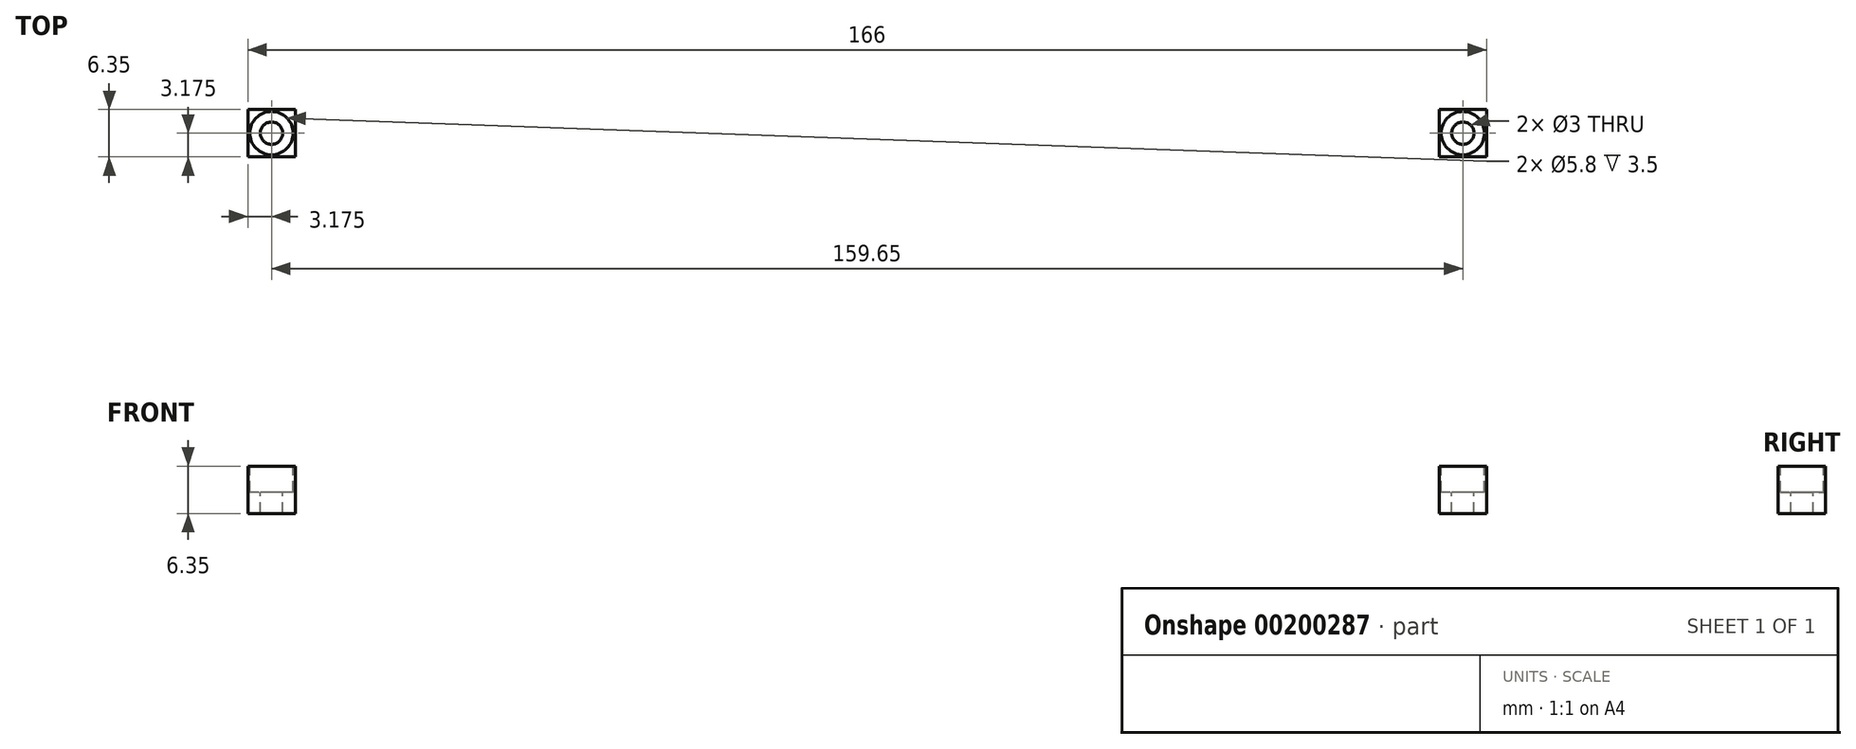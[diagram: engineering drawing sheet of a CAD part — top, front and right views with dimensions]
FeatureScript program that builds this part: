
annotation { "Feature Type Name" : "Feature", "Feature Type Description" : "" }
export const myFeature = defineFeature(function(context is Context, id is Id, definition is map)
    precondition{}
    {
        {
            var Q0;
            Q0=qCreatedBy(makeId("Top.planeOp"),FACE);
            var sketch = newSketch(context, id + "F0", { "sketchPlane" : qUnion([Q0])});
            skLineSegment(sketch, "E0.bottom", {"start": v(83, -21.5) * mm, "end": v(-83, -21.5) * mm});
            skPoint(sketch, "E0.middle", {"position": v(0, 0) * mm});
            skLineSegment(sketch, "E1.top", {"start": v(72.5, 14.5) * mm, "end": v(71.5, 14.5) * mm});
            skLineSegment(sketch, "E2", {"start": v(66.5, 14.5) * mm, "end": v(66.5, 12.75) * mm});
            skLineSegment(sketch, "E3", {"start": v(-72.5, 14.5) * mm, "end": v(-72.5, 12.75) * mm});
            skLineSegment(sketch, "E4", {"start": v(-71.5, 14.5) * mm, "end": v(-71.5, 12.75) * mm});
            skLineSegment(sketch, "E5", {"start": v(-66.5, 14.5) * mm, "end": v(-66.5, 12.75) * mm});
            skLineSegment(sketch, "E6", {"start": v(-65.5, 14.5) * mm, "end": v(-65.5, 12.75) * mm});
            skLineSegment(sketch, "E7", {"start": v(-60.5, 14.5) * mm, "end": v(-60.5, 12.75) * mm});
            skLineSegment(sketch, "E8", {"start": v(-59.5, 14.5) * mm, "end": v(-59.5, 12.75) * mm});
            skLineSegment(sketch, "E9", {"start": v(-54.5, 14.5) * mm, "end": v(-54.5, 12.75) * mm});
            skLineSegment(sketch, "E10", {"start": v(-53.5, 14.5) * mm, "end": v(-53.5, 12.75) * mm});
            skLineSegment(sketch, "E11", {"start": v(-48.5, 14.5) * mm, "end": v(-48.5, 12.75) * mm});
            skLineSegment(sketch, "E12", {"start": v(-47.5, 14.5) * mm, "end": v(-47.5, 12.75) * mm});
            skLineSegment(sketch, "E13", {"start": v(-42.5, 14.5) * mm, "end": v(-42.5, 12.75) * mm});
            skLineSegment(sketch, "E14", {"start": v(-41.5, 14.5) * mm, "end": v(-41.5, 12.75) * mm});
            skLineSegment(sketch, "E15", {"start": v(-36.5, 14.5) * mm, "end": v(-36.5, 12.75) * mm});
            skLineSegment(sketch, "E16", {"start": v(-35.5, 14.5) * mm, "end": v(-35.5, 12.75) * mm});
            skLineSegment(sketch, "E17", {"start": v(-30.5, 14.5) * mm, "end": v(-30.5, 12.75) * mm});
            skLineSegment(sketch, "E18", {"start": v(-29.5, 14.5) * mm, "end": v(-29.5, 12.75) * mm});
            skLineSegment(sketch, "E19", {"start": v(-24.5, 14.5) * mm, "end": v(-24.5, 12.75) * mm});
            skLineSegment(sketch, "E20", {"start": v(-23.5, 14.5) * mm, "end": v(-23.5, 12.75) * mm});
            skLineSegment(sketch, "E21", {"start": v(-18.5, 14.5) * mm, "end": v(-18.5, 12.75) * mm});
            skLineSegment(sketch, "E22", {"start": v(-17.5, 14.5) * mm, "end": v(-17.5, 12.75) * mm});
            skLineSegment(sketch, "E23", {"start": v(-12.5, 14.5) * mm, "end": v(-12.5, 12.75) * mm});
            skLineSegment(sketch, "E24", {"start": v(-11.5, 14.5) * mm, "end": v(-11.5, 12.75) * mm});
            skLineSegment(sketch, "E25", {"start": v(-6.5, 14.5) * mm, "end": v(-6.5, 12.75) * mm});
            skLineSegment(sketch, "E26", {"start": v(-5.5, 14.5) * mm, "end": v(-5.5, 12.75) * mm});
            skLineSegment(sketch, "E27", {"start": v(-0.5, 14.5) * mm, "end": v(-0.5, 12.75) * mm});
            skLineSegment(sketch, "E28", {"start": v(0.5, 14.5) * mm, "end": v(0.5, 12.75) * mm});
            skLineSegment(sketch, "E29", {"start": v(5.5, 14.5) * mm, "end": v(5.5, 12.75) * mm});
            skLineSegment(sketch, "E30", {"start": v(6.5, 14.5) * mm, "end": v(6.5, 12.75) * mm});
            skLineSegment(sketch, "E31", {"start": v(11.5, 14.5) * mm, "end": v(11.5, 12.75) * mm});
            skLineSegment(sketch, "E32", {"start": v(12.5, 14.5) * mm, "end": v(12.5, 12.75) * mm});
            skLineSegment(sketch, "E33", {"start": v(17.5, 14.5) * mm, "end": v(17.5, 12.75) * mm});
            skLineSegment(sketch, "E34", {"start": v(18.5, 14.5) * mm, "end": v(18.5, 12.75) * mm});
            skLineSegment(sketch, "E35", {"start": v(23.5, 14.5) * mm, "end": v(23.5, 12.75) * mm});
            skLineSegment(sketch, "E36", {"start": v(24.5, 14.5) * mm, "end": v(24.5, 12.75) * mm});
            skLineSegment(sketch, "E37", {"start": v(29.5, 14.5) * mm, "end": v(29.5, 12.75) * mm});
            skLineSegment(sketch, "E38", {"start": v(30.5, 14.5) * mm, "end": v(30.5, 12.75) * mm});
            skLineSegment(sketch, "E39", {"start": v(35.5, 14.5) * mm, "end": v(35.5, 12.75) * mm});
            skLineSegment(sketch, "E40", {"start": v(36.5, 14.5) * mm, "end": v(36.5, 12.75) * mm});
            skLineSegment(sketch, "E41", {"start": v(42.5, 14.5) * mm, "end": v(42.5, 12.75) * mm});
            skLineSegment(sketch, "E42", {"start": v(47.5, 14.5) * mm, "end": v(47.5, 12.75) * mm});
            skLineSegment(sketch, "E43", {"start": v(53.5, 14.5) * mm, "end": v(53.5, 12.75) * mm});
            skLineSegment(sketch, "E44", {"start": v(54.5, 14.5) * mm, "end": v(54.5, 12.75) * mm});
            skLineSegment(sketch, "E45", {"start": v(60.5, 14.5) * mm, "end": v(60.5, 12.75) * mm});
            skLineSegment(sketch, "E46", {"start": v(65.5, 14.5) * mm, "end": v(65.5, 12.75) * mm});
            skLineSegment(sketch, "E47", {"start": v(41.5, 14.5) * mm, "end": v(41.5, 12.75) * mm});
            skLineSegment(sketch, "E48", {"start": v(48.5, 14.5) * mm, "end": v(48.5, 12.75) * mm});
            skLineSegment(sketch, "E49", {"start": v(59.5, 14.5) * mm, "end": v(59.5, 12.75) * mm});
            skLineSegment(sketch, "E50", {"start": v(71.5, 14.5) * mm, "end": v(71.5, 12.75) * mm});
            skLineSegment(sketch, "E51", {"start": v(72.5, 14.5) * mm, "end": v(72.5, 12.75) * mm});
            skLineSegment(sketch, "E52.trimOffspring", {"start": v(-72.5, -12.75) * mm, "end": v(-72.5, -14.5) * mm});
            skLineSegment(sketch, "E53.trimOffspring", {"start": v(-71.5, -12.75) * mm, "end": v(-71.5, -14.5) * mm});
            skLineSegment(sketch, "E54.trimOffspring", {"start": v(-66.5, -12.75) * mm, "end": v(-66.5, -14.5) * mm});
            skLineSegment(sketch, "E55.trimOffspring", {"start": v(-65.5, -12.75) * mm, "end": v(-65.5, -14.5) * mm});
            skLineSegment(sketch, "E56.trimOffspring", {"start": v(-60.5, -12.75) * mm, "end": v(-60.5, -14.5) * mm});
            skLineSegment(sketch, "E57.trimOffspring", {"start": v(-59.5, -12.75) * mm, "end": v(-59.5, -14.5) * mm});
            skLineSegment(sketch, "E58.trimOffspring", {"start": v(-54.5, -12.75) * mm, "end": v(-54.5, -14.5) * mm});
            skLineSegment(sketch, "E59.trimOffspring", {"start": v(-53.5, -12.75) * mm, "end": v(-53.5, -14.5) * mm});
            skLineSegment(sketch, "E60.trimOffspring", {"start": v(-48.5, -12.75) * mm, "end": v(-48.5, -14.5) * mm});
            skLineSegment(sketch, "E61.trimOffspring", {"start": v(-47.5, -12.75) * mm, "end": v(-47.5, -14.5) * mm});
            skLineSegment(sketch, "E62.trimOffspring", {"start": v(-42.5, -12.75) * mm, "end": v(-42.5, -14.5) * mm});
            skLineSegment(sketch, "E63.trimOffspring", {"start": v(-41.5, -12.75) * mm, "end": v(-41.5, -14.5) * mm});
            skLineSegment(sketch, "E64.trimOffspring", {"start": v(-36.5, -12.75) * mm, "end": v(-36.5, -14.5) * mm});
            skLineSegment(sketch, "E65.trimOffspring", {"start": v(-35.5, -12.75) * mm, "end": v(-35.5, -14.5) * mm});
            skLineSegment(sketch, "E66.trimOffspring", {"start": v(-30.5, -12.75) * mm, "end": v(-30.5, -14.5) * mm});
            skLineSegment(sketch, "E67.trimOffspring", {"start": v(-29.5, -12.75) * mm, "end": v(-29.5, -14.5) * mm});
            skLineSegment(sketch, "E68.trimOffspring", {"start": v(-24.5, -12.75) * mm, "end": v(-24.5, -14.5) * mm});
            skLineSegment(sketch, "E69.trimOffspring", {"start": v(-23.5, -12.75) * mm, "end": v(-23.5, -14.5) * mm});
            skLineSegment(sketch, "E70.trimOffspring", {"start": v(-18.5, -12.75) * mm, "end": v(-18.5, -14.5) * mm});
            skLineSegment(sketch, "E71.trimOffspring", {"start": v(-17.5, -12.75) * mm, "end": v(-17.5, -14.5) * mm});
            skLineSegment(sketch, "E72.trimOffspring", {"start": v(-12.5, -12.75) * mm, "end": v(-12.5, -14.5) * mm});
            skLineSegment(sketch, "E73.trimOffspring", {"start": v(-11.5, -12.75) * mm, "end": v(-11.5, -14.5) * mm});
            skLineSegment(sketch, "E74.trimOffspring", {"start": v(-6.5, -12.75) * mm, "end": v(-6.5, -14.5) * mm});
            skLineSegment(sketch, "E75.trimOffspring", {"start": v(-5.5, -12.75) * mm, "end": v(-5.5, -14.5) * mm});
            skLineSegment(sketch, "E76.trimOffspring", {"start": v(-0.5, -12.75) * mm, "end": v(-0.5, -14.5) * mm});
            skLineSegment(sketch, "E77.trimOffspring", {"start": v(0.5, -12.75) * mm, "end": v(0.5, -14.5) * mm});
            skLineSegment(sketch, "E78.trimOffspring", {"start": v(5.5, -12.75) * mm, "end": v(5.5, -14.5) * mm});
            skLineSegment(sketch, "E79.trimOffspring", {"start": v(6.5, -12.75) * mm, "end": v(6.5, -14.5) * mm});
            skLineSegment(sketch, "E80.trimOffspring", {"start": v(11.5, -12.75) * mm, "end": v(11.5, -14.5) * mm});
            skLineSegment(sketch, "E81.trimOffspring", {"start": v(12.5, -12.75) * mm, "end": v(12.5, -14.5) * mm});
            skLineSegment(sketch, "E82.trimOffspring", {"start": v(17.5, -12.75) * mm, "end": v(17.5, -14.5) * mm});
            skLineSegment(sketch, "E83.trimOffspring", {"start": v(18.5, -12.75) * mm, "end": v(18.5, -14.5) * mm});
            skLineSegment(sketch, "E84.trimOffspring", {"start": v(23.5, -12.75) * mm, "end": v(23.5, -14.5) * mm});
            skLineSegment(sketch, "E85.trimOffspring", {"start": v(24.5, -12.75) * mm, "end": v(24.5, -14.5) * mm});
            skLineSegment(sketch, "E86.trimOffspring", {"start": v(29.5, -12.75) * mm, "end": v(29.5, -14.5) * mm});
            skLineSegment(sketch, "E87.trimOffspring", {"start": v(30.5, -12.75) * mm, "end": v(30.5, -14.5) * mm});
            skLineSegment(sketch, "E88.trimOffspring", {"start": v(35.5, -12.75) * mm, "end": v(35.5, -14.5) * mm});
            skLineSegment(sketch, "E89.trimOffspring", {"start": v(36.5, -12.75) * mm, "end": v(36.5, -14.5) * mm});
            skLineSegment(sketch, "E90.trimOffspring", {"start": v(41.5, -12.75) * mm, "end": v(41.5, -14.5) * mm});
            skLineSegment(sketch, "E91.trimOffspring", {"start": v(42.5, -12.75) * mm, "end": v(42.5, -14.5) * mm});
            skLineSegment(sketch, "E92.trimOffspring", {"start": v(47.5, -12.75) * mm, "end": v(47.5, -14.5) * mm});
            skLineSegment(sketch, "E93.trimOffspring", {"start": v(48.5, -12.75) * mm, "end": v(48.5, -14.5) * mm});
            skLineSegment(sketch, "E94.trimOffspring", {"start": v(53.5, -12.75) * mm, "end": v(53.5, -14.5) * mm});
            skLineSegment(sketch, "E95.trimOffspring", {"start": v(54.5, -12.75) * mm, "end": v(54.5, -14.5) * mm});
            skLineSegment(sketch, "E96.trimOffspring", {"start": v(59.5, -12.75) * mm, "end": v(59.5, -14.5) * mm});
            skLineSegment(sketch, "E97.trimOffspring", {"start": v(60.5, -12.75) * mm, "end": v(60.5, -14.5) * mm});
            skLineSegment(sketch, "E98.trimOffspring", {"start": v(65.5, -12.75) * mm, "end": v(65.5, -14.5) * mm});
            skLineSegment(sketch, "E99.trimOffspring", {"start": v(66.5, -12.75) * mm, "end": v(66.5, -14.5) * mm});
            skLineSegment(sketch, "E100.trimOffspring", {"start": v(71.5, -12.75) * mm, "end": v(71.5, -14.5) * mm});
            skLineSegment(sketch, "E101.trimOffspring", {"start": v(72.5, -12.75) * mm, "end": v(72.5, -14.5) * mm});
            skLineSegment(sketch, "E102.trimOffspring", {"start": v(66.5, 12.75) * mm, "end": v(71.5, 12.75) * mm});
            skLineSegment(sketch, "E103.trimOffspring", {"start": v(60.5, 12.75) * mm, "end": v(65.5, 12.75) * mm});
            skLineSegment(sketch, "E104.trimOffspring", {"start": v(54.5, 12.75) * mm, "end": v(59.5, 12.75) * mm});
            skLineSegment(sketch, "E105.trimOffspring", {"start": v(48.5, 12.75) * mm, "end": v(53.5, 12.75) * mm});
            skLineSegment(sketch, "E106.trimOffspring", {"start": v(42.5, 12.75) * mm, "end": v(47.5, 12.75) * mm});
            skLineSegment(sketch, "E107.trimOffspring", {"start": v(36.5, 12.75) * mm, "end": v(41.5, 12.75) * mm});
            skLineSegment(sketch, "E108.trimOffspring", {"start": v(30.5, 12.75) * mm, "end": v(35.5, 12.75) * mm});
            skLineSegment(sketch, "E109.trimOffspring", {"start": v(24.5, 12.75) * mm, "end": v(29.5, 12.75) * mm});
            skLineSegment(sketch, "E110.trimOffspring", {"start": v(18.5, 12.75) * mm, "end": v(23.5, 12.75) * mm});
            skLineSegment(sketch, "E111.trimOffspring", {"start": v(12.5, 12.75) * mm, "end": v(17.5, 12.75) * mm});
            skLineSegment(sketch, "E112.trimOffspring", {"start": v(6.5, 12.75) * mm, "end": v(11.5, 12.75) * mm});
            skLineSegment(sketch, "E113.trimOffspring", {"start": v(0.5, 12.75) * mm, "end": v(5.5, 12.75) * mm});
            skLineSegment(sketch, "E114.trimOffspring", {"start": v(-5.5, 12.75) * mm, "end": v(-0.5, 12.75) * mm});
            skLineSegment(sketch, "E115.trimOffspring", {"start": v(-11.5, 12.75) * mm, "end": v(-6.5, 12.75) * mm});
            skLineSegment(sketch, "E116.trimOffspring", {"start": v(-17.5, 12.75) * mm, "end": v(-12.5, 12.75) * mm});
            skLineSegment(sketch, "E117.trimOffspring", {"start": v(-23.5, 12.75) * mm, "end": v(-18.5, 12.75) * mm});
            skLineSegment(sketch, "E118.trimOffspring", {"start": v(-29.5, 12.75) * mm, "end": v(-24.5, 12.75) * mm});
            skLineSegment(sketch, "E119.trimOffspring", {"start": v(-35.5, 12.75) * mm, "end": v(-30.5, 12.75) * mm});
            skLineSegment(sketch, "E120.trimOffspring", {"start": v(-41.5, 12.75) * mm, "end": v(-36.5, 12.75) * mm});
            skLineSegment(sketch, "E121.trimOffspring", {"start": v(-47.5, 12.75) * mm, "end": v(-42.5, 12.75) * mm});
            skLineSegment(sketch, "E122.trimOffspring", {"start": v(-53.5, 12.75) * mm, "end": v(-48.5, 12.75) * mm});
            skLineSegment(sketch, "E123.trimOffspring", {"start": v(-59.5, 12.75) * mm, "end": v(-54.5, 12.75) * mm});
            skLineSegment(sketch, "E124.trimOffspring", {"start": v(-65.5, 12.75) * mm, "end": v(-60.5, 12.75) * mm});
            skLineSegment(sketch, "E125.trimOffspring", {"start": v(-71.5, 12.75) * mm, "end": v(-66.5, 12.75) * mm});
            skLineSegment(sketch, "E126.trimOffspring", {"start": v(-71.5, -12.75) * mm, "end": v(-66.5, -12.75) * mm});
            skLineSegment(sketch, "E127.trimOffspring", {"start": v(-71.5, -14.5) * mm, "end": v(-72.5, -14.5) * mm});
            skLineSegment(sketch, "E128.trimOffspring", {"start": v(-65.5, -12.75) * mm, "end": v(-60.5, -12.75) * mm});
            skLineSegment(sketch, "E129.trimOffspring", {"start": v(-65.5, -14.5) * mm, "end": v(-66.5, -14.5) * mm});
            skLineSegment(sketch, "E130.trimOffspring", {"start": v(-59.5, -12.75) * mm, "end": v(-54.5, -12.75) * mm});
            skLineSegment(sketch, "E131.trimOffspring", {"start": v(-59.5, -14.5) * mm, "end": v(-60.5, -14.5) * mm});
            skLineSegment(sketch, "E132.trimOffspring", {"start": v(-53.5, -12.75) * mm, "end": v(-48.5, -12.75) * mm});
            skLineSegment(sketch, "E133.trimOffspring", {"start": v(-53.5, -14.5) * mm, "end": v(-54.5, -14.5) * mm});
            skLineSegment(sketch, "E134.trimOffspring", {"start": v(-47.5, -12.75) * mm, "end": v(-42.5, -12.75) * mm});
            skLineSegment(sketch, "E135.trimOffspring", {"start": v(-47.5, -14.5) * mm, "end": v(-48.5, -14.5) * mm});
            skLineSegment(sketch, "E136.trimOffspring", {"start": v(-41.5, -12.75) * mm, "end": v(-36.5, -12.75) * mm});
            skLineSegment(sketch, "E137.trimOffspring", {"start": v(-41.5, -14.5) * mm, "end": v(-42.5, -14.5) * mm});
            skLineSegment(sketch, "E138.trimOffspring", {"start": v(-35.5, -12.75) * mm, "end": v(-30.5, -12.75) * mm});
            skLineSegment(sketch, "E139.trimOffspring", {"start": v(-35.5, -14.5) * mm, "end": v(-36.5, -14.5) * mm});
            skLineSegment(sketch, "E140.trimOffspring", {"start": v(-29.5, -12.75) * mm, "end": v(-24.5, -12.75) * mm});
            skLineSegment(sketch, "E141.trimOffspring", {"start": v(-29.5, -14.5) * mm, "end": v(-30.5, -14.5) * mm});
            skLineSegment(sketch, "E142.trimOffspring", {"start": v(-23.5, -12.75) * mm, "end": v(-18.5, -12.75) * mm});
            skLineSegment(sketch, "E143.trimOffspring", {"start": v(-23.5, -14.5) * mm, "end": v(-24.5, -14.5) * mm});
            skLineSegment(sketch, "E144.trimOffspring", {"start": v(-17.5, -12.75) * mm, "end": v(-12.5, -12.75) * mm});
            skLineSegment(sketch, "E145.trimOffspring", {"start": v(-17.5, -14.5) * mm, "end": v(-18.5, -14.5) * mm});
            skLineSegment(sketch, "E146.trimOffspring", {"start": v(-11.5, -12.75) * mm, "end": v(-6.5, -12.75) * mm});
            skLineSegment(sketch, "E147.trimOffspring", {"start": v(-11.5, -14.5) * mm, "end": v(-12.5, -14.5) * mm});
            skLineSegment(sketch, "E148.trimOffspring", {"start": v(-5.5, -12.75) * mm, "end": v(-0.5, -12.75) * mm});
            skLineSegment(sketch, "E149.trimOffspring", {"start": v(-5.5, -14.5) * mm, "end": v(-6.5, -14.5) * mm});
            skLineSegment(sketch, "E150.trimOffspring", {"start": v(0.5, -12.75) * mm, "end": v(5.5, -12.75) * mm});
            skLineSegment(sketch, "E151.trimOffspring", {"start": v(0.5, -14.5) * mm, "end": v(-0.5, -14.5) * mm});
            skLineSegment(sketch, "E152.trimOffspring", {"start": v(6.5, -12.75) * mm, "end": v(11.5, -12.75) * mm});
            skLineSegment(sketch, "E153.trimOffspring", {"start": v(6.5, -14.5) * mm, "end": v(5.5, -14.5) * mm});
            skLineSegment(sketch, "E154.trimOffspring", {"start": v(12.5, -12.75) * mm, "end": v(17.5, -12.75) * mm});
            skLineSegment(sketch, "E155.trimOffspring", {"start": v(12.5, -14.5) * mm, "end": v(11.5, -14.5) * mm});
            skLineSegment(sketch, "E156.trimOffspring", {"start": v(18.5, -12.75) * mm, "end": v(23.5, -12.75) * mm});
            skLineSegment(sketch, "E157.trimOffspring", {"start": v(24.5, -12.75) * mm, "end": v(29.5, -12.75) * mm});
            skLineSegment(sketch, "E158.trimOffspring", {"start": v(30.5, -12.75) * mm, "end": v(35.5, -12.75) * mm});
            skLineSegment(sketch, "E159.trimOffspring", {"start": v(36.5, -12.75) * mm, "end": v(41.5, -12.75) * mm});
            skLineSegment(sketch, "E160.trimOffspring", {"start": v(42.5, -12.75) * mm, "end": v(47.5, -12.75) * mm});
            skLineSegment(sketch, "E161.trimOffspring", {"start": v(48.5, -12.75) * mm, "end": v(53.5, -12.75) * mm});
            skLineSegment(sketch, "E162.trimOffspring", {"start": v(54.5, -12.75) * mm, "end": v(59.5, -12.75) * mm});
            skLineSegment(sketch, "E163.trimOffspring", {"start": v(60.5, -12.75) * mm, "end": v(65.5, -12.75) * mm});
            skLineSegment(sketch, "E164.trimOffspring", {"start": v(66.5, -12.75) * mm, "end": v(71.5, -12.75) * mm});
            skLineSegment(sketch, "E165.trimOffspring", {"start": v(66.5, -14.5) * mm, "end": v(65.5, -14.5) * mm});
            skLineSegment(sketch, "E166.trimOffspring", {"start": v(60.5, -14.5) * mm, "end": v(59.5, -14.5) * mm});
            skLineSegment(sketch, "E167", {"start": v(71.5, -14.5) * mm, "end": v(72.5, -14.5) * mm});
            skLineSegment(sketch, "E168.trimOffspring", {"start": v(54.5, -14.5) * mm, "end": v(53.5, -14.5) * mm});
            skLineSegment(sketch, "E169.trimOffspring", {"start": v(48.5, -14.5) * mm, "end": v(47.5, -14.5) * mm});
            skLineSegment(sketch, "E170.trimOffspring", {"start": v(42.5, -14.5) * mm, "end": v(41.5, -14.5) * mm});
            skLineSegment(sketch, "E171.trimOffspring", {"start": v(36.5, -14.5) * mm, "end": v(35.5, -14.5) * mm});
            skLineSegment(sketch, "E172.trimOffspring", {"start": v(30.5, -14.5) * mm, "end": v(29.5, -14.5) * mm});
            skLineSegment(sketch, "E173.trimOffspring", {"start": v(24.5, -14.5) * mm, "end": v(23.5, -14.5) * mm});
            skLineSegment(sketch, "E174.trimOffspring", {"start": v(18.5, -14.5) * mm, "end": v(17.5, -14.5) * mm});
            skLineSegment(sketch, "E175.trimOffspring", {"start": v(-71.5, 14.5) * mm, "end": v(-72.5, 14.5) * mm});
            skLineSegment(sketch, "E176.trimOffspring", {"start": v(-65.5, 14.5) * mm, "end": v(-66.5, 14.5) * mm});
            skLineSegment(sketch, "E177.trimOffspring", {"start": v(-59.5, 14.5) * mm, "end": v(-60.5, 14.5) * mm});
            skLineSegment(sketch, "E178.trimOffspring", {"start": v(-53.5, 14.5) * mm, "end": v(-54.5, 14.5) * mm});
            skLineSegment(sketch, "E179.trimOffspring", {"start": v(-47.5, 14.5) * mm, "end": v(-48.5, 14.5) * mm});
            skLineSegment(sketch, "E180.trimOffspring", {"start": v(-41.5, 14.5) * mm, "end": v(-42.5, 14.5) * mm});
            skLineSegment(sketch, "E181.trimOffspring", {"start": v(-35.5, 14.5) * mm, "end": v(-36.5, 14.5) * mm});
            skLineSegment(sketch, "E182.trimOffspring", {"start": v(-29.5, 14.5) * mm, "end": v(-30.5, 14.5) * mm});
            skLineSegment(sketch, "E183.trimOffspring", {"start": v(-23.5, 14.5) * mm, "end": v(-24.5, 14.5) * mm});
            skLineSegment(sketch, "E184.trimOffspring", {"start": v(-17.5, 14.5) * mm, "end": v(-18.5, 14.5) * mm});
            skLineSegment(sketch, "E185.trimOffspring", {"start": v(-11.5, 14.5) * mm, "end": v(-12.5, 14.5) * mm});
            skLineSegment(sketch, "E186.trimOffspring", {"start": v(-5.5, 14.5) * mm, "end": v(-6.5, 14.5) * mm});
            skLineSegment(sketch, "E187.trimOffspring", {"start": v(0.5, 14.5) * mm, "end": v(-0.5, 14.5) * mm});
            skLineSegment(sketch, "E188.trimOffspring", {"start": v(12.5, 14.5) * mm, "end": v(11.5, 14.5) * mm});
            skLineSegment(sketch, "E189.trimOffspring", {"start": v(18.5, 14.5) * mm, "end": v(17.5, 14.5) * mm});
            skLineSegment(sketch, "E190.trimOffspring", {"start": v(24.5, 14.5) * mm, "end": v(23.5, 14.5) * mm});
            skLineSegment(sketch, "E191.trimOffspring", {"start": v(30.5, 14.5) * mm, "end": v(29.5, 14.5) * mm});
            skLineSegment(sketch, "E192.trimOffspring", {"start": v(66.5, 14.5) * mm, "end": v(65.5, 14.5) * mm});
            skLineSegment(sketch, "E193.trimOffspring", {"start": v(60.5, 14.5) * mm, "end": v(59.5, 14.5) * mm});
            skLineSegment(sketch, "E194.trimOffspring", {"start": v(54.5, 14.5) * mm, "end": v(53.5, 14.5) * mm});
            skLineSegment(sketch, "E195.trimOffspring", {"start": v(48.5, 14.5) * mm, "end": v(47.5, 14.5) * mm});
            skLineSegment(sketch, "E196.trimOffspring", {"start": v(42.5, 14.5) * mm, "end": v(41.5, 14.5) * mm});
            skLineSegment(sketch, "E197.trimOffspring", {"start": v(36.5, 14.5) * mm, "end": v(35.5, 14.5) * mm});
            skPoint(sketch, "E198", {"position": v(0, 4.75) * mm});
            skPoint(sketch, "E199", {"position": v(0, -4.75) * mm});
            skLineSegment(sketch, "E200", {"start": v(5.5, 14.5) * mm, "end": v(6.5, 14.5) * mm});
            skLineSegment(sketch, "E201", {"start": v(-83, 21.5) * mm, "end": v(-83, -21.5) * mm});
            skLineSegment(sketch, "E202", {"start": v(83, 21.5) * mm, "end": v(83, -21.5) * mm});
            skLineSegment(sketch, "E203", {"start": v(-83, 21.5) * mm, "end": v(83, 21.5) * mm});
            skLineSegment(sketch, "E204", {"start": v(-76.65, 12.75) * mm, "end": v(-76.65, -12.75) * mm});
            skLineSegment(sketch, "E205", {"start": v(76.65, 12.75) * mm, "end": v(76.65, -12.75) * mm});
            skLineSegment(sketch, "E206", {"start": v(-72.5, 12.75) * mm, "end": v(-76.65, 12.75) * mm});
            skLineSegment(sketch, "E207", {"start": v(-72.5, -12.75) * mm, "end": v(-76.65, -12.75) * mm});
            skLineSegment(sketch, "E208", {"start": v(72.5, 12.75) * mm, "end": v(76.65, 12.75) * mm});
            skLineSegment(sketch, "E209", {"start": v(72.5, -12.75) * mm, "end": v(76.65, -12.75) * mm});
            skPoint(sketch, "E210.orphan", {"position": v(-76.65, 21.5) * mm});
            skPoint(sketch, "E211.orphan", {"position": v(76.65, 21.5) * mm});
            skLineSegment(sketch, "E212.bottom", {"start": v(-83, 21.5) * mm, "end": v(-76.65, 21.5) * mm});
            skLineSegment(sketch, "E212.top", {"start": v(-83, 15.15) * mm, "end": v(-76.65, 15.15) * mm});
            skLineSegment(sketch, "E212.left", {"start": v(-83, 21.5) * mm, "end": v(-83, 15.15) * mm});
            skLineSegment(sketch, "E212.right", {"start": v(-76.65, 21.5) * mm, "end": v(-76.65, 15.15) * mm});
            skLineSegment(sketch, "E213.bottom", {"start": v(-83, -21.5) * mm, "end": v(-76.65, -21.5) * mm});
            skLineSegment(sketch, "E213.top", {"start": v(-83, -15.15) * mm, "end": v(-76.65, -15.15) * mm});
            skLineSegment(sketch, "E213.left", {"start": v(-83, -21.5) * mm, "end": v(-83, -15.15) * mm});
            skLineSegment(sketch, "E213.right", {"start": v(-76.65, -21.5) * mm, "end": v(-76.65, -15.15) * mm});
            skLineSegment(sketch, "E214.bottom", {"start": v(83, 21.5) * mm, "end": v(76.65, 21.5) * mm});
            skLineSegment(sketch, "E214.top", {"start": v(83, 15.15) * mm, "end": v(76.65, 15.15) * mm});
            skLineSegment(sketch, "E214.left", {"start": v(83, 21.5) * mm, "end": v(83, 15.15) * mm});
            skLineSegment(sketch, "E214.right", {"start": v(76.65, 21.5) * mm, "end": v(76.65, 15.15) * mm});
            skLineSegment(sketch, "E215.bottom", {"start": v(83, -21.5) * mm, "end": v(76.65, -21.5) * mm});
            skLineSegment(sketch, "E215.top", {"start": v(83, -15.15) * mm, "end": v(76.65, -15.15) * mm});
            skLineSegment(sketch, "E215.left", {"start": v(83, -21.5) * mm, "end": v(83, -15.15) * mm});
            skLineSegment(sketch, "E215.right", {"start": v(76.65, -21.5) * mm, "end": v(76.65, -15.15) * mm});
            skPoint(sketch, "E216", {"position": v(-79.83, 18.32) * mm});
            skPoint(sketch, "E216.positionSnap0", {"position": v(-83, 18.32) * mm});
            skPoint(sketch, "E216.positionSnap1", {"position": v(-79.83, 21.5) * mm});
            skPoint(sketch, "E217", {"position": v(-79.82, -18.33) * mm});
            skPoint(sketch, "E217.positionSnap0", {"position": v(-83, -18.33) * mm});
            skPoint(sketch, "E217.positionSnap1", {"position": v(-79.82, -21.5) * mm});
            skPoint(sketch, "E218", {"position": v(79.83, 18.33) * mm});
            skPoint(sketch, "E218.positionSnap0", {"position": v(79.83, 21.5) * mm});
            skPoint(sketch, "E218.positionSnap1", {"position": v(83, 18.33) * mm});
            skPoint(sketch, "E219", {"position": v(79.83, -18.32) * mm});
            skPoint(sketch, "E219.positionSnap0", {"position": v(79.83, -21.5) * mm});
            skPoint(sketch, "E219.positionSnap1", {"position": v(83, -18.32) * mm});
            skSolve(sketch);
        }
        {
            var Q0;
            Q0=makeQuery(id+"F0.imprint","IMPRINT",FACE,{"disambiguationData":[TD([[makeQuery(id+"F0.imprint","IMPRINT",EDGE,{"derivedFrom":sQuery(id+"F0.wireOp",EDGE,"E0.bottom")}),-1.0]])]});
            var Q1;
            Q1=makeQuery(id+"F0.imprint","IMPRINT",FACE,{"disambiguationData":[TD([[makeQuery(id+"F0.imprint","IMPRINT",EDGE,{"derivedFrom":sQuery(id+"F0.wireOp",EDGE,"K6HQALcg-SJ6E-UbpV-g3pM-SsoFJaYyiFHH.bottom")}),-1.0]])]});
            var Q2;
            Q2=makeQuery(id+"F0.imprint","IMPRINT",FACE,{"disambiguationData":[TD([[makeQuery(id+"F0.imprint","IMPRINT",EDGE,{"derivedFrom":sQuery(id+"F0.wireOp",EDGE,"uAhlTMjh-OfK6-l1ir-Uiju-3nNvoJU6ebrF.bottom")}),1.0]])]});
            var Q3;
            Q3=makeQuery(id+"F0.imprint","IMPRINT",FACE,{"disambiguationData":[TD([[makeQuery(id+"F0.imprint","IMPRINT",EDGE,{"derivedFrom":sQuery(id+"F0.wireOp",EDGE,"429Vr5qv-e7wW-sgXi-vds3-SuZLJVXfNGyf.bottom")}),1.0]])]});
            var Q4;
            Q4=makeQuery(id+"F0.imprint","IMPRINT",FACE,{"disambiguationData":[TD([[makeQuery(id+"F0.imprint","IMPRINT",EDGE,{"derivedFrom":sQuery(id+"F0.wireOp",EDGE,"gyryeJMz-dnlH-ok6h-gJO2-PR3vbfRycGDr.bottom")}),-1.0]])]});
            var Q5;
            Q5=makeQuery(id+"F0.imprint","IMPRINT",FACE,{"disambiguationData":[TD([[makeQuery(id+"F0.imprint","IMPRINT",EDGE,{"derivedFrom":sQuery(id+"F0.wireOp",EDGE,"Y8WRlr66-7ynR-SeF8-deyW-E6T64acYDO3Z")}),-1.0]])]});
            var Q6;
            Q6=makeQuery(id+"F0.imprint","IMPRINT",FACE,{"disambiguationData":[TD([[makeQuery(id+"F0.imprint","IMPRINT",EDGE,{"derivedFrom":sQuery(id+"F0.wireOp",EDGE,"CmYglgzX-7el8-TEhF-yuX0-v4MmdMN9OrBr")}),-1.0]])]});
            var Q7;
            Q7=makeQuery(id+"F0.imprint","IMPRINT",FACE,{"disambiguationData":[TD([[makeQuery(id+"F0.imprint","IMPRINT",EDGE,{"derivedFrom":sQuery(id+"F0.wireOp",EDGE,"HYskgT41-gjKB-VkVM-H0Av-PifG51DztXFj")}),1.0]])]});
            var Q8;
            Q8=makeQuery(id+"F0.imprint","IMPRINT",FACE,{"disambiguationData":[TD([[makeQuery(id+"F0.imprint","IMPRINT",EDGE,{"derivedFrom":sQuery(id+"F0.wireOp",EDGE,"VJJEuZ6N-K9C8-7fmf-kXEK-6F0NHCstAFbI")}),1.0]])]});
            var Q9;
            Q9=makeQuery(id+"F0.imprint","IMPRINT",FACE,{"disambiguationData":[TD([[makeQuery(id+"F0.imprint","IMPRINT",EDGE,{"derivedFrom":sQuery(id+"F0.wireOp",EDGE,"E212.bottom")}),-1.0]])]});
            var Q10;
            Q10=makeQuery(id+"F0.imprint","IMPRINT",FACE,{"disambiguationData":[TD([[makeQuery(id+"F0.imprint","IMPRINT",EDGE,{"derivedFrom":sQuery(id+"F0.wireOp",EDGE,"E213.bottom")}),1.0]])]});
            var Q11;
            Q11=makeQuery(id+"F0.imprint","IMPRINT",FACE,{"disambiguationData":[TD([[makeQuery(id+"F0.imprint","IMPRINT",EDGE,{"derivedFrom":sQuery(id+"F0.wireOp",EDGE,"E215.bottom")}),-1.0]])]});
            var Q12;
            Q12=makeQuery(id+"F0.imprint","IMPRINT",FACE,{"disambiguationData":[TD([[makeQuery(id+"F0.imprint","IMPRINT",EDGE,{"derivedFrom":sQuery(id+"F0.wireOp",EDGE,"E214.bottom")}),1.0]])]});
            extrude(context, id + "F1", {"entities" : qUnion([Q0, Q1, Q2, Q3, Q4, Q5, Q6, Q7, Q8, Q9, Q10, Q11, Q12]), "oppositeDirection" : true, "depth" : 6.35 * mm});
        }
        {
            var Q0;
            Q0=sQuery(id+"F0.wireOp",VERTEX,"E216");
            var Q1;
            Q1=sQuery(id+"F0.wireOp",VERTEX,"E217");
            var Q2;
            Q2=sQuery(id+"F0.wireOp",VERTEX,"E218");
            var Q3;
            Q3=sQuery(id+"F0.wireOp",VERTEX,"E219");
            var Q4;
            Q4=makeQuery(id+"F1.opExtrude","SWEPT_BODY",BODY,{"disambiguationData":[OSD([sQuery(id+"F0.wireOp",EDGE,"E0.bottom"),sQuery(id+"F0.wireOp",EDGE,"E1.top"),sQuery(id+"F0.wireOp",EDGE,"E2"),sQuery(id+"F0.wireOp",EDGE,"E3"),sQuery(id+"F0.wireOp",EDGE,"E4"),sQuery(id+"F0.wireOp",EDGE,"E5"),sQuery(id+"F0.wireOp",EDGE,"E6"),sQuery(id+"F0.wireOp",EDGE,"E7"),sQuery(id+"F0.wireOp",EDGE,"E8"),sQuery(id+"F0.wireOp",EDGE,"E9"),sQuery(id+"F0.wireOp",EDGE,"E10"),sQuery(id+"F0.wireOp",EDGE,"E11"),sQuery(id+"F0.wireOp",EDGE,"E12"),sQuery(id+"F0.wireOp",EDGE,"E13"),sQuery(id+"F0.wireOp",EDGE,"E14"),sQuery(id+"F0.wireOp",EDGE,"E15"),sQuery(id+"F0.wireOp",EDGE,"E16"),sQuery(id+"F0.wireOp",EDGE,"E17"),sQuery(id+"F0.wireOp",EDGE,"E18"),sQuery(id+"F0.wireOp",EDGE,"E19"),sQuery(id+"F0.wireOp",EDGE,"E20"),sQuery(id+"F0.wireOp",EDGE,"E21"),sQuery(id+"F0.wireOp",EDGE,"E22"),sQuery(id+"F0.wireOp",EDGE,"E23"),sQuery(id+"F0.wireOp",EDGE,"E24"),sQuery(id+"F0.wireOp",EDGE,"E25"),sQuery(id+"F0.wireOp",EDGE,"E26"),sQuery(id+"F0.wireOp",EDGE,"E27"),sQuery(id+"F0.wireOp",EDGE,"E28"),sQuery(id+"F0.wireOp",EDGE,"E29"),sQuery(id+"F0.wireOp",EDGE,"E30"),sQuery(id+"F0.wireOp",EDGE,"E31"),sQuery(id+"F0.wireOp",EDGE,"E32"),sQuery(id+"F0.wireOp",EDGE,"E33"),sQuery(id+"F0.wireOp",EDGE,"E34"),sQuery(id+"F0.wireOp",EDGE,"E35"),sQuery(id+"F0.wireOp",EDGE,"E36"),sQuery(id+"F0.wireOp",EDGE,"E37"),sQuery(id+"F0.wireOp",EDGE,"E38"),sQuery(id+"F0.wireOp",EDGE,"E39"),sQuery(id+"F0.wireOp",EDGE,"E40"),sQuery(id+"F0.wireOp",EDGE,"E41"),sQuery(id+"F0.wireOp",EDGE,"E42"),sQuery(id+"F0.wireOp",EDGE,"E43"),sQuery(id+"F0.wireOp",EDGE,"E44"),sQuery(id+"F0.wireOp",EDGE,"E45"),sQuery(id+"F0.wireOp",EDGE,"E46"),sQuery(id+"F0.wireOp",EDGE,"E47"),sQuery(id+"F0.wireOp",EDGE,"E48"),sQuery(id+"F0.wireOp",EDGE,"E49"),sQuery(id+"F0.wireOp",EDGE,"E50"),sQuery(id+"F0.wireOp",EDGE,"E51"),sQuery(id+"F0.wireOp",EDGE,"E52.trimOffspring"),sQuery(id+"F0.wireOp",EDGE,"E53.trimOffspring"),sQuery(id+"F0.wireOp",EDGE,"E54.trimOffspring"),sQuery(id+"F0.wireOp",EDGE,"E55.trimOffspring"),sQuery(id+"F0.wireOp",EDGE,"E56.trimOffspring"),sQuery(id+"F0.wireOp",EDGE,"E57.trimOffspring"),sQuery(id+"F0.wireOp",EDGE,"E58.trimOffspring"),sQuery(id+"F0.wireOp",EDGE,"E59.trimOffspring"),sQuery(id+"F0.wireOp",EDGE,"E60.trimOffspring"),sQuery(id+"F0.wireOp",EDGE,"E61.trimOffspring"),sQuery(id+"F0.wireOp",EDGE,"E62.trimOffspring"),sQuery(id+"F0.wireOp",EDGE,"E63.trimOffspring"),sQuery(id+"F0.wireOp",EDGE,"E64.trimOffspring"),sQuery(id+"F0.wireOp",EDGE,"E65.trimOffspring"),sQuery(id+"F0.wireOp",EDGE,"E66.trimOffspring"),sQuery(id+"F0.wireOp",EDGE,"E67.trimOffspring"),sQuery(id+"F0.wireOp",EDGE,"E68.trimOffspring"),sQuery(id+"F0.wireOp",EDGE,"E69.trimOffspring"),sQuery(id+"F0.wireOp",EDGE,"E70.trimOffspring"),sQuery(id+"F0.wireOp",EDGE,"E71.trimOffspring"),sQuery(id+"F0.wireOp",EDGE,"E72.trimOffspring"),sQuery(id+"F0.wireOp",EDGE,"E73.trimOffspring"),sQuery(id+"F0.wireOp",EDGE,"E74.trimOffspring"),sQuery(id+"F0.wireOp",EDGE,"E75.trimOffspring"),sQuery(id+"F0.wireOp",EDGE,"E76.trimOffspring"),sQuery(id+"F0.wireOp",EDGE,"E77.trimOffspring"),sQuery(id+"F0.wireOp",EDGE,"E78.trimOffspring"),sQuery(id+"F0.wireOp",EDGE,"E79.trimOffspring"),sQuery(id+"F0.wireOp",EDGE,"E80.trimOffspring"),sQuery(id+"F0.wireOp",EDGE,"E81.trimOffspring"),sQuery(id+"F0.wireOp",EDGE,"E82.trimOffspring"),sQuery(id+"F0.wireOp",EDGE,"E83.trimOffspring"),sQuery(id+"F0.wireOp",EDGE,"E84.trimOffspring"),sQuery(id+"F0.wireOp",EDGE,"E85.trimOffspring"),sQuery(id+"F0.wireOp",EDGE,"E86.trimOffspring"),sQuery(id+"F0.wireOp",EDGE,"E87.trimOffspring"),sQuery(id+"F0.wireOp",EDGE,"E88.trimOffspring"),sQuery(id+"F0.wireOp",EDGE,"E89.trimOffspring"),sQuery(id+"F0.wireOp",EDGE,"E90.trimOffspring"),sQuery(id+"F0.wireOp",EDGE,"E91.trimOffspring"),sQuery(id+"F0.wireOp",EDGE,"E92.trimOffspring"),sQuery(id+"F0.wireOp",EDGE,"E93.trimOffspring"),sQuery(id+"F0.wireOp",EDGE,"E94.trimOffspring"),sQuery(id+"F0.wireOp",EDGE,"E95.trimOffspring"),sQuery(id+"F0.wireOp",EDGE,"E96.trimOffspring"),sQuery(id+"F0.wireOp",EDGE,"E97.trimOffspring"),sQuery(id+"F0.wireOp",EDGE,"E98.trimOffspring"),sQuery(id+"F0.wireOp",EDGE,"E99.trimOffspring"),sQuery(id+"F0.wireOp",EDGE,"E100.trimOffspring"),sQuery(id+"F0.wireOp",EDGE,"E101.trimOffspring"),sQuery(id+"F0.wireOp",EDGE,"E102.trimOffspring"),sQuery(id+"F0.wireOp",EDGE,"E103.trimOffspring"),sQuery(id+"F0.wireOp",EDGE,"E104.trimOffspring"),sQuery(id+"F0.wireOp",EDGE,"E105.trimOffspring"),sQuery(id+"F0.wireOp",EDGE,"E106.trimOffspring"),sQuery(id+"F0.wireOp",EDGE,"E107.trimOffspring"),sQuery(id+"F0.wireOp",EDGE,"E108.trimOffspring"),sQuery(id+"F0.wireOp",EDGE,"E109.trimOffspring"),sQuery(id+"F0.wireOp",EDGE,"E110.trimOffspring"),sQuery(id+"F0.wireOp",EDGE,"E111.trimOffspring"),sQuery(id+"F0.wireOp",EDGE,"E112.trimOffspring"),sQuery(id+"F0.wireOp",EDGE,"E113.trimOffspring"),sQuery(id+"F0.wireOp",EDGE,"E114.trimOffspring"),sQuery(id+"F0.wireOp",EDGE,"E115.trimOffspring"),sQuery(id+"F0.wireOp",EDGE,"E116.trimOffspring"),sQuery(id+"F0.wireOp",EDGE,"E117.trimOffspring"),sQuery(id+"F0.wireOp",EDGE,"E118.trimOffspring"),sQuery(id+"F0.wireOp",EDGE,"E119.trimOffspring"),sQuery(id+"F0.wireOp",EDGE,"E120.trimOffspring"),sQuery(id+"F0.wireOp",EDGE,"E121.trimOffspring"),sQuery(id+"F0.wireOp",EDGE,"E122.trimOffspring"),sQuery(id+"F0.wireOp",EDGE,"E123.trimOffspring"),sQuery(id+"F0.wireOp",EDGE,"E124.trimOffspring"),sQuery(id+"F0.wireOp",EDGE,"E125.trimOffspring"),sQuery(id+"F0.wireOp",EDGE,"E126.trimOffspring"),sQuery(id+"F0.wireOp",EDGE,"E127.trimOffspring"),sQuery(id+"F0.wireOp",EDGE,"E128.trimOffspring"),sQuery(id+"F0.wireOp",EDGE,"E129.trimOffspring"),sQuery(id+"F0.wireOp",EDGE,"E130.trimOffspring"),sQuery(id+"F0.wireOp",EDGE,"E131.trimOffspring"),sQuery(id+"F0.wireOp",EDGE,"E132.trimOffspring"),sQuery(id+"F0.wireOp",EDGE,"E133.trimOffspring"),sQuery(id+"F0.wireOp",EDGE,"E134.trimOffspring"),sQuery(id+"F0.wireOp",EDGE,"E135.trimOffspring"),sQuery(id+"F0.wireOp",EDGE,"E136.trimOffspring"),sQuery(id+"F0.wireOp",EDGE,"E137.trimOffspring"),sQuery(id+"F0.wireOp",EDGE,"E138.trimOffspring"),sQuery(id+"F0.wireOp",EDGE,"E139.trimOffspring"),sQuery(id+"F0.wireOp",EDGE,"E140.trimOffspring"),sQuery(id+"F0.wireOp",EDGE,"E141.trimOffspring"),sQuery(id+"F0.wireOp",EDGE,"E142.trimOffspring"),sQuery(id+"F0.wireOp",EDGE,"E143.trimOffspring"),sQuery(id+"F0.wireOp",EDGE,"E144.trimOffspring"),sQuery(id+"F0.wireOp",EDGE,"E145.trimOffspring"),sQuery(id+"F0.wireOp",EDGE,"E146.trimOffspring"),sQuery(id+"F0.wireOp",EDGE,"E147.trimOffspring"),sQuery(id+"F0.wireOp",EDGE,"E148.trimOffspring"),sQuery(id+"F0.wireOp",EDGE,"E149.trimOffspring"),sQuery(id+"F0.wireOp",EDGE,"E150.trimOffspring"),sQuery(id+"F0.wireOp",EDGE,"E151.trimOffspring"),sQuery(id+"F0.wireOp",EDGE,"E152.trimOffspring"),sQuery(id+"F0.wireOp",EDGE,"E153.trimOffspring"),sQuery(id+"F0.wireOp",EDGE,"E154.trimOffspring"),sQuery(id+"F0.wireOp",EDGE,"E155.trimOffspring"),sQuery(id+"F0.wireOp",EDGE,"E156.trimOffspring"),sQuery(id+"F0.wireOp",EDGE,"E157.trimOffspring"),sQuery(id+"F0.wireOp",EDGE,"E158.trimOffspring"),sQuery(id+"F0.wireOp",EDGE,"E159.trimOffspring"),sQuery(id+"F0.wireOp",EDGE,"E160.trimOffspring"),sQuery(id+"F0.wireOp",EDGE,"E161.trimOffspring"),sQuery(id+"F0.wireOp",EDGE,"E162.trimOffspring"),sQuery(id+"F0.wireOp",EDGE,"E163.trimOffspring"),sQuery(id+"F0.wireOp",EDGE,"E164.trimOffspring"),sQuery(id+"F0.wireOp",EDGE,"E165.trimOffspring"),sQuery(id+"F0.wireOp",EDGE,"E166.trimOffspring"),sQuery(id+"F0.wireOp",EDGE,"E167"),sQuery(id+"F0.wireOp",EDGE,"E168.trimOffspring"),sQuery(id+"F0.wireOp",EDGE,"E169.trimOffspring"),sQuery(id+"F0.wireOp",EDGE,"E170.trimOffspring"),sQuery(id+"F0.wireOp",EDGE,"E171.trimOffspring"),sQuery(id+"F0.wireOp",EDGE,"E172.trimOffspring"),sQuery(id+"F0.wireOp",EDGE,"E173.trimOffspring"),sQuery(id+"F0.wireOp",EDGE,"E174.trimOffspring"),sQuery(id+"F0.wireOp",EDGE,"E175.trimOffspring"),sQuery(id+"F0.wireOp",EDGE,"E176.trimOffspring"),sQuery(id+"F0.wireOp",EDGE,"E177.trimOffspring"),sQuery(id+"F0.wireOp",EDGE,"E178.trimOffspring"),sQuery(id+"F0.wireOp",EDGE,"E179.trimOffspring"),sQuery(id+"F0.wireOp",EDGE,"E180.trimOffspring"),sQuery(id+"F0.wireOp",EDGE,"E181.trimOffspring"),sQuery(id+"F0.wireOp",EDGE,"E182.trimOffspring"),sQuery(id+"F0.wireOp",EDGE,"E183.trimOffspring"),sQuery(id+"F0.wireOp",EDGE,"E184.trimOffspring"),sQuery(id+"F0.wireOp",EDGE,"E185.trimOffspring"),sQuery(id+"F0.wireOp",EDGE,"E186.trimOffspring"),sQuery(id+"F0.wireOp",EDGE,"E187.trimOffspring"),sQuery(id+"F0.wireOp",EDGE,"E188.trimOffspring"),sQuery(id+"F0.wireOp",EDGE,"E189.trimOffspring"),sQuery(id+"F0.wireOp",EDGE,"E190.trimOffspring"),sQuery(id+"F0.wireOp",EDGE,"E191.trimOffspring"),sQuery(id+"F0.wireOp",EDGE,"E192.trimOffspring"),sQuery(id+"F0.wireOp",EDGE,"E193.trimOffspring"),sQuery(id+"F0.wireOp",EDGE,"E194.trimOffspring"),sQuery(id+"F0.wireOp",EDGE,"E195.trimOffspring"),sQuery(id+"F0.wireOp",EDGE,"E196.trimOffspring"),sQuery(id+"F0.wireOp",EDGE,"E197.trimOffspring"),sQuery(id+"F0.wireOp",EDGE,"E200"),sQuery(id+"F0.wireOp",EDGE,"E201"),sQuery(id+"F0.wireOp",EDGE,"E202"),sQuery(id+"F0.wireOp",EDGE,"E203"),sQuery(id+"F0.wireOp",EDGE,"E204"),sQuery(id+"F0.wireOp",EDGE,"E205"),sQuery(id+"F0.wireOp",EDGE,"E206"),sQuery(id+"F0.wireOp",EDGE,"E207"),sQuery(id+"F0.wireOp",EDGE,"E208"),sQuery(id+"F0.wireOp",EDGE,"E209"),sQuery(id+"F0.wireOp",EDGE,"E212.bottom"),sQuery(id+"F0.wireOp",EDGE,"E212.left"),sQuery(id+"F0.wireOp",EDGE,"E213.bottom"),sQuery(id+"F0.wireOp",EDGE,"E213.left"),sQuery(id+"F0.wireOp",EDGE,"E214.bottom"),sQuery(id+"F0.wireOp",EDGE,"E214.left"),sQuery(id+"F0.wireOp",EDGE,"E215.bottom"),sQuery(id+"F0.wireOp",EDGE,"E215.left")])]});
            hole(context, id + "F2", {"style" : HoleStyle.C_BORE, "endStyle" : HoleEndStyle.BLIND, "standardTappedOrClearance" : lookupTablePath({ "standard" : "ISO", "size" : "3", "type" : "Drilled" }), "standardBlindInLast" : lookupTablePath({ "standard" : "ISO", "size" : "3", "type" : "Drilled" }), "holeDiameter" : 3 * mm, "cBoreDiameter" : 5.8 * mm, "cBoreDepth" : 3.5 * mm, "holeDepth" : 8 * mm, "startFromSketch" : true, "locations" : qUnion([Q0, Q1, Q2, Q3]), "scope" : qUnion([Q4]), "majorDiameter" : 5 * mm, "tappedDepth" : 12 * mm, "tapClearance" : 3});
        }
        {
            var Q0;
            Q0=makeQuery(id+"F1.opExtrude","CAP_FACE",FACE,{"disambiguationData":[OSD([sQuery(id+"F0.wireOp",EDGE,"E0.bottom"),sQuery(id+"F0.wireOp",EDGE,"E1.top"),sQuery(id+"F0.wireOp",EDGE,"E2"),sQuery(id+"F0.wireOp",EDGE,"E3"),sQuery(id+"F0.wireOp",EDGE,"E4"),sQuery(id+"F0.wireOp",EDGE,"E5"),sQuery(id+"F0.wireOp",EDGE,"E6"),sQuery(id+"F0.wireOp",EDGE,"E7"),sQuery(id+"F0.wireOp",EDGE,"E8"),sQuery(id+"F0.wireOp",EDGE,"E9"),sQuery(id+"F0.wireOp",EDGE,"E10"),sQuery(id+"F0.wireOp",EDGE,"E11"),sQuery(id+"F0.wireOp",EDGE,"E12"),sQuery(id+"F0.wireOp",EDGE,"E13"),sQuery(id+"F0.wireOp",EDGE,"E14"),sQuery(id+"F0.wireOp",EDGE,"E15"),sQuery(id+"F0.wireOp",EDGE,"E16"),sQuery(id+"F0.wireOp",EDGE,"E17"),sQuery(id+"F0.wireOp",EDGE,"E18"),sQuery(id+"F0.wireOp",EDGE,"E19"),sQuery(id+"F0.wireOp",EDGE,"E20"),sQuery(id+"F0.wireOp",EDGE,"E21"),sQuery(id+"F0.wireOp",EDGE,"E22"),sQuery(id+"F0.wireOp",EDGE,"E23"),sQuery(id+"F0.wireOp",EDGE,"E24"),sQuery(id+"F0.wireOp",EDGE,"E25"),sQuery(id+"F0.wireOp",EDGE,"E26"),sQuery(id+"F0.wireOp",EDGE,"E27"),sQuery(id+"F0.wireOp",EDGE,"E28"),sQuery(id+"F0.wireOp",EDGE,"E29"),sQuery(id+"F0.wireOp",EDGE,"E30"),sQuery(id+"F0.wireOp",EDGE,"E31"),sQuery(id+"F0.wireOp",EDGE,"E32"),sQuery(id+"F0.wireOp",EDGE,"E33"),sQuery(id+"F0.wireOp",EDGE,"E34"),sQuery(id+"F0.wireOp",EDGE,"E35"),sQuery(id+"F0.wireOp",EDGE,"E36"),sQuery(id+"F0.wireOp",EDGE,"E37"),sQuery(id+"F0.wireOp",EDGE,"E38"),sQuery(id+"F0.wireOp",EDGE,"E39"),sQuery(id+"F0.wireOp",EDGE,"E40"),sQuery(id+"F0.wireOp",EDGE,"E41"),sQuery(id+"F0.wireOp",EDGE,"E42"),sQuery(id+"F0.wireOp",EDGE,"E43"),sQuery(id+"F0.wireOp",EDGE,"E44"),sQuery(id+"F0.wireOp",EDGE,"E45"),sQuery(id+"F0.wireOp",EDGE,"E46"),sQuery(id+"F0.wireOp",EDGE,"E47"),sQuery(id+"F0.wireOp",EDGE,"E48"),sQuery(id+"F0.wireOp",EDGE,"E49"),sQuery(id+"F0.wireOp",EDGE,"E50"),sQuery(id+"F0.wireOp",EDGE,"E51"),sQuery(id+"F0.wireOp",EDGE,"E52.trimOffspring"),sQuery(id+"F0.wireOp",EDGE,"E53.trimOffspring"),sQuery(id+"F0.wireOp",EDGE,"E54.trimOffspring"),sQuery(id+"F0.wireOp",EDGE,"E55.trimOffspring"),sQuery(id+"F0.wireOp",EDGE,"E56.trimOffspring"),sQuery(id+"F0.wireOp",EDGE,"E57.trimOffspring"),sQuery(id+"F0.wireOp",EDGE,"E58.trimOffspring"),sQuery(id+"F0.wireOp",EDGE,"E59.trimOffspring"),sQuery(id+"F0.wireOp",EDGE,"E60.trimOffspring"),sQuery(id+"F0.wireOp",EDGE,"E61.trimOffspring"),sQuery(id+"F0.wireOp",EDGE,"E62.trimOffspring"),sQuery(id+"F0.wireOp",EDGE,"E63.trimOffspring"),sQuery(id+"F0.wireOp",EDGE,"E64.trimOffspring"),sQuery(id+"F0.wireOp",EDGE,"E65.trimOffspring"),sQuery(id+"F0.wireOp",EDGE,"E66.trimOffspring"),sQuery(id+"F0.wireOp",EDGE,"E67.trimOffspring"),sQuery(id+"F0.wireOp",EDGE,"E68.trimOffspring"),sQuery(id+"F0.wireOp",EDGE,"E69.trimOffspring"),sQuery(id+"F0.wireOp",EDGE,"E70.trimOffspring"),sQuery(id+"F0.wireOp",EDGE,"E71.trimOffspring"),sQuery(id+"F0.wireOp",EDGE,"E72.trimOffspring"),sQuery(id+"F0.wireOp",EDGE,"E73.trimOffspring"),sQuery(id+"F0.wireOp",EDGE,"E74.trimOffspring"),sQuery(id+"F0.wireOp",EDGE,"E75.trimOffspring"),sQuery(id+"F0.wireOp",EDGE,"E76.trimOffspring"),sQuery(id+"F0.wireOp",EDGE,"E77.trimOffspring"),sQuery(id+"F0.wireOp",EDGE,"E78.trimOffspring"),sQuery(id+"F0.wireOp",EDGE,"E79.trimOffspring"),sQuery(id+"F0.wireOp",EDGE,"E80.trimOffspring"),sQuery(id+"F0.wireOp",EDGE,"E81.trimOffspring"),sQuery(id+"F0.wireOp",EDGE,"E82.trimOffspring"),sQuery(id+"F0.wireOp",EDGE,"E83.trimOffspring"),sQuery(id+"F0.wireOp",EDGE,"E84.trimOffspring"),sQuery(id+"F0.wireOp",EDGE,"E85.trimOffspring"),sQuery(id+"F0.wireOp",EDGE,"E86.trimOffspring"),sQuery(id+"F0.wireOp",EDGE,"E87.trimOffspring"),sQuery(id+"F0.wireOp",EDGE,"E88.trimOffspring"),sQuery(id+"F0.wireOp",EDGE,"E89.trimOffspring"),sQuery(id+"F0.wireOp",EDGE,"E90.trimOffspring"),sQuery(id+"F0.wireOp",EDGE,"E91.trimOffspring"),sQuery(id+"F0.wireOp",EDGE,"E92.trimOffspring"),sQuery(id+"F0.wireOp",EDGE,"E93.trimOffspring"),sQuery(id+"F0.wireOp",EDGE,"E94.trimOffspring"),sQuery(id+"F0.wireOp",EDGE,"E95.trimOffspring"),sQuery(id+"F0.wireOp",EDGE,"E96.trimOffspring"),sQuery(id+"F0.wireOp",EDGE,"E97.trimOffspring"),sQuery(id+"F0.wireOp",EDGE,"E98.trimOffspring"),sQuery(id+"F0.wireOp",EDGE,"E99.trimOffspring"),sQuery(id+"F0.wireOp",EDGE,"E100.trimOffspring"),sQuery(id+"F0.wireOp",EDGE,"E101.trimOffspring"),sQuery(id+"F0.wireOp",EDGE,"E102.trimOffspring"),sQuery(id+"F0.wireOp",EDGE,"E103.trimOffspring"),sQuery(id+"F0.wireOp",EDGE,"E104.trimOffspring"),sQuery(id+"F0.wireOp",EDGE,"E105.trimOffspring"),sQuery(id+"F0.wireOp",EDGE,"E106.trimOffspring"),sQuery(id+"F0.wireOp",EDGE,"E107.trimOffspring"),sQuery(id+"F0.wireOp",EDGE,"E108.trimOffspring"),sQuery(id+"F0.wireOp",EDGE,"E109.trimOffspring"),sQuery(id+"F0.wireOp",EDGE,"E110.trimOffspring"),sQuery(id+"F0.wireOp",EDGE,"E111.trimOffspring"),sQuery(id+"F0.wireOp",EDGE,"E112.trimOffspring"),sQuery(id+"F0.wireOp",EDGE,"E113.trimOffspring"),sQuery(id+"F0.wireOp",EDGE,"E114.trimOffspring"),sQuery(id+"F0.wireOp",EDGE,"E115.trimOffspring"),sQuery(id+"F0.wireOp",EDGE,"E116.trimOffspring"),sQuery(id+"F0.wireOp",EDGE,"E117.trimOffspring"),sQuery(id+"F0.wireOp",EDGE,"E118.trimOffspring"),sQuery(id+"F0.wireOp",EDGE,"E119.trimOffspring"),sQuery(id+"F0.wireOp",EDGE,"E120.trimOffspring"),sQuery(id+"F0.wireOp",EDGE,"E121.trimOffspring"),sQuery(id+"F0.wireOp",EDGE,"E122.trimOffspring"),sQuery(id+"F0.wireOp",EDGE,"E123.trimOffspring"),sQuery(id+"F0.wireOp",EDGE,"E124.trimOffspring"),sQuery(id+"F0.wireOp",EDGE,"E125.trimOffspring"),sQuery(id+"F0.wireOp",EDGE,"E126.trimOffspring"),sQuery(id+"F0.wireOp",EDGE,"E127.trimOffspring"),sQuery(id+"F0.wireOp",EDGE,"E128.trimOffspring"),sQuery(id+"F0.wireOp",EDGE,"E129.trimOffspring"),sQuery(id+"F0.wireOp",EDGE,"E130.trimOffspring"),sQuery(id+"F0.wireOp",EDGE,"E131.trimOffspring"),sQuery(id+"F0.wireOp",EDGE,"E132.trimOffspring"),sQuery(id+"F0.wireOp",EDGE,"E133.trimOffspring"),sQuery(id+"F0.wireOp",EDGE,"E134.trimOffspring"),sQuery(id+"F0.wireOp",EDGE,"E135.trimOffspring"),sQuery(id+"F0.wireOp",EDGE,"E136.trimOffspring"),sQuery(id+"F0.wireOp",EDGE,"E137.trimOffspring"),sQuery(id+"F0.wireOp",EDGE,"E138.trimOffspring"),sQuery(id+"F0.wireOp",EDGE,"E139.trimOffspring"),sQuery(id+"F0.wireOp",EDGE,"E140.trimOffspring"),sQuery(id+"F0.wireOp",EDGE,"E141.trimOffspring"),sQuery(id+"F0.wireOp",EDGE,"E142.trimOffspring"),sQuery(id+"F0.wireOp",EDGE,"E143.trimOffspring"),sQuery(id+"F0.wireOp",EDGE,"E144.trimOffspring"),sQuery(id+"F0.wireOp",EDGE,"E145.trimOffspring"),sQuery(id+"F0.wireOp",EDGE,"E146.trimOffspring"),sQuery(id+"F0.wireOp",EDGE,"E147.trimOffspring"),sQuery(id+"F0.wireOp",EDGE,"E148.trimOffspring"),sQuery(id+"F0.wireOp",EDGE,"E149.trimOffspring"),sQuery(id+"F0.wireOp",EDGE,"E150.trimOffspring"),sQuery(id+"F0.wireOp",EDGE,"E151.trimOffspring"),sQuery(id+"F0.wireOp",EDGE,"E152.trimOffspring"),sQuery(id+"F0.wireOp",EDGE,"E153.trimOffspring"),sQuery(id+"F0.wireOp",EDGE,"E154.trimOffspring"),sQuery(id+"F0.wireOp",EDGE,"E155.trimOffspring"),sQuery(id+"F0.wireOp",EDGE,"E156.trimOffspring"),sQuery(id+"F0.wireOp",EDGE,"E157.trimOffspring"),sQuery(id+"F0.wireOp",EDGE,"E158.trimOffspring"),sQuery(id+"F0.wireOp",EDGE,"E159.trimOffspring"),sQuery(id+"F0.wireOp",EDGE,"E160.trimOffspring"),sQuery(id+"F0.wireOp",EDGE,"E161.trimOffspring"),sQuery(id+"F0.wireOp",EDGE,"E162.trimOffspring"),sQuery(id+"F0.wireOp",EDGE,"E163.trimOffspring"),sQuery(id+"F0.wireOp",EDGE,"E164.trimOffspring"),sQuery(id+"F0.wireOp",EDGE,"E165.trimOffspring"),sQuery(id+"F0.wireOp",EDGE,"E166.trimOffspring"),sQuery(id+"F0.wireOp",EDGE,"E167"),sQuery(id+"F0.wireOp",EDGE,"E168.trimOffspring"),sQuery(id+"F0.wireOp",EDGE,"E169.trimOffspring"),sQuery(id+"F0.wireOp",EDGE,"E170.trimOffspring"),sQuery(id+"F0.wireOp",EDGE,"E171.trimOffspring"),sQuery(id+"F0.wireOp",EDGE,"E172.trimOffspring"),sQuery(id+"F0.wireOp",EDGE,"E173.trimOffspring"),sQuery(id+"F0.wireOp",EDGE,"E174.trimOffspring"),sQuery(id+"F0.wireOp",EDGE,"E175.trimOffspring"),sQuery(id+"F0.wireOp",EDGE,"E176.trimOffspring"),sQuery(id+"F0.wireOp",EDGE,"E177.trimOffspring"),sQuery(id+"F0.wireOp",EDGE,"E178.trimOffspring"),sQuery(id+"F0.wireOp",EDGE,"E179.trimOffspring"),sQuery(id+"F0.wireOp",EDGE,"E180.trimOffspring"),sQuery(id+"F0.wireOp",EDGE,"E181.trimOffspring"),sQuery(id+"F0.wireOp",EDGE,"E182.trimOffspring"),sQuery(id+"F0.wireOp",EDGE,"E183.trimOffspring"),sQuery(id+"F0.wireOp",EDGE,"E184.trimOffspring"),sQuery(id+"F0.wireOp",EDGE,"E185.trimOffspring"),sQuery(id+"F0.wireOp",EDGE,"E186.trimOffspring"),sQuery(id+"F0.wireOp",EDGE,"E187.trimOffspring"),sQuery(id+"F0.wireOp",EDGE,"E188.trimOffspring"),sQuery(id+"F0.wireOp",EDGE,"E189.trimOffspring"),sQuery(id+"F0.wireOp",EDGE,"E190.trimOffspring"),sQuery(id+"F0.wireOp",EDGE,"E191.trimOffspring"),sQuery(id+"F0.wireOp",EDGE,"E192.trimOffspring"),sQuery(id+"F0.wireOp",EDGE,"E193.trimOffspring"),sQuery(id+"F0.wireOp",EDGE,"E194.trimOffspring"),sQuery(id+"F0.wireOp",EDGE,"E195.trimOffspring"),sQuery(id+"F0.wireOp",EDGE,"E196.trimOffspring"),sQuery(id+"F0.wireOp",EDGE,"E197.trimOffspring"),sQuery(id+"F0.wireOp",EDGE,"E200"),sQuery(id+"F0.wireOp",EDGE,"E201"),sQuery(id+"F0.wireOp",EDGE,"E202"),sQuery(id+"F0.wireOp",EDGE,"E203"),sQuery(id+"F0.wireOp",EDGE,"E204"),sQuery(id+"F0.wireOp",EDGE,"E205"),sQuery(id+"F0.wireOp",EDGE,"E206"),sQuery(id+"F0.wireOp",EDGE,"E207"),sQuery(id+"F0.wireOp",EDGE,"E208"),sQuery(id+"F0.wireOp",EDGE,"E209"),sQuery(id+"F0.wireOp",EDGE,"E212.bottom"),sQuery(id+"F0.wireOp",EDGE,"E212.left"),sQuery(id+"F0.wireOp",EDGE,"E213.bottom"),sQuery(id+"F0.wireOp",EDGE,"E213.left"),sQuery(id+"F0.wireOp",EDGE,"E214.bottom"),sQuery(id+"F0.wireOp",EDGE,"E214.left"),sQuery(id+"F0.wireOp",EDGE,"E215.bottom"),sQuery(id+"F0.wireOp",EDGE,"E215.left")])],"isStart":false});
            var sketch = newSketch(context, id + "F3", { "sketchPlane" : qUnion([Q0])});
            skPoint(sketch, "E220", {"position": v(-76.65, 0) * mm});
            skPoint(sketch, "E221", {"position": v(-76.65, 3.18) * mm});
            skPoint(sketch, "E222", {"position": v(-76.65, -3.17) * mm});
            skLineSegment(sketch, "E223.bottom", {"start": v(-76.65, 3.18) * mm, "end": v(-80.15, 3.18) * mm});
            skLineSegment(sketch, "E223.top", {"start": v(-76.65, -3.17) * mm, "end": v(-80.15, -3.17) * mm});
            skLineSegment(sketch, "E223.left", {"start": v(-76.65, 3.18) * mm, "end": v(-76.65, -3.17) * mm});
            skLineSegment(sketch, "E223.right", {"start": v(-80.15, 3.18) * mm, "end": v(-80.15, -3.17) * mm});
            skPoint(sketch, "E224", {"position": v(76.65, 3.18) * mm});
            skLineSegment(sketch, "E225.bottom", {"start": v(76.65, 3.18) * mm, "end": v(80.15, 3.18) * mm});
            skLineSegment(sketch, "E225.top", {"start": v(76.65, -3.17) * mm, "end": v(80.15, -3.17) * mm});
            skLineSegment(sketch, "E225.left", {"start": v(76.65, 3.18) * mm, "end": v(76.65, -3.17) * mm});
            skLineSegment(sketch, "E225.right", {"start": v(80.15, 3.18) * mm, "end": v(80.15, -3.17) * mm});
            skSolve(sketch);
        }
        {
            var Q0;
            Q0 = qSketchRegion(id + "F3", true);
            var Q1;
            Q1=makeQuery(id+"F3.imprint","IMPRINT",FACE,{"disambiguationData":[TD([[makeQuery(id+"F3.imprint","IMPRINT",EDGE,{"derivedFrom":sQuery(id+"F3.wireOp",EDGE,"E223.bottom")}),1.0]])]});
            extrude(context, id + "F4", {"entities" : qUnion([Q0, Q1]), "operationType" : NewBodyOperationType.REMOVE, "oppositeDirection" : true, "depth" : 4.85 * mm, "offsetDistance" : 25 * mm});
        }
    });
